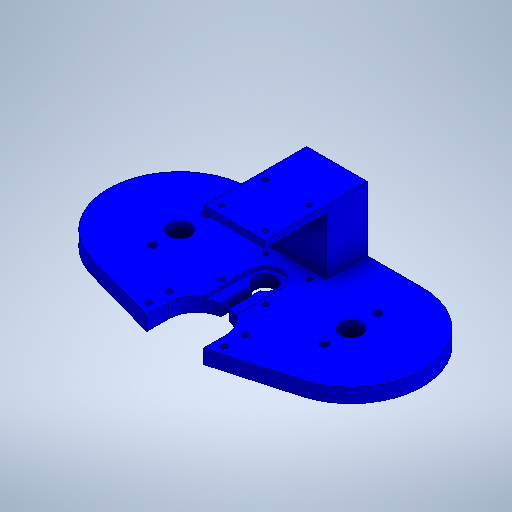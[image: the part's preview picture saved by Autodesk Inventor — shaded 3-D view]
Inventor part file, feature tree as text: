
AUTODESK INVENTOR PART (.ipt)
format: ipt  version: 2025.2 (Build 292293000, 293)  size: 375,808 bytes
history: native  units: mm
features: extrude x6, hole x4, sketch x3, other x1
ambient origin geometry x8: Origin, YZ Plane, XZ Plane, XY Plane, X Axis, Y Axis, Z Axis, Center Point
bodies: Body1 (feature_tree)
feature tree (14):
  sketch  "Sketch6"  dims[d37=120.0mm d38=60.0mm]
  extrude  "Extrusion8"  Depth=60.0mm
  hole  "Hole1"  [1 undecoded]
  hole  "Hole2"  [1 undecoded]
  extrude  "Extrusion10"  Depth=8.0mm
  extrude  "Extrusion11"  Depth=10.0mm TaperAngle=0.0deg
  extrude  "Extrusion12"  Depth=8.0mm
  extrude  "Extrusion13"  Depth=8.0mm
  other  "Work Axis1"
  hole  "Hole3"  [1 undecoded]
  extrude  "Extrusion14"  Depth=8.0mm
  hole  "Hole4"  [1 undecoded]
  sketch  "Sketch7"  dims[d39=100.0mm d40=100.0mm]
  sketch  "Sketch8"  dims[d41=15.0mm d42=15.0mm d43=15.0mm d44=10.0mm d45=0.0mm d46=37.3mm d47=37.3mm d48=30.759mm d49=30.759mm d50=30.759mm d51=3.5mm d52=6.0mm d53=4.0mm d54=2.0mm d55=90.0deg d56=8.0mm d57=20.594885mm d58=5.0mm d59=6.0mm d60=4.0mm d61=2.0mm d62=90.0deg d63=8.0mm d64=20.594885mm d65=42.3mm d66=43.0mm d67=50.0mm d70=6.0mm d71=200.0mm d72=15.0mm d73=0.0mm d74=45.0mm d75=0.0mm d76=22.5mm d77=200.0mm d78=2.0mm d79=0.0mm d80=5.0mm d81=43.0mm d82=0.0mm d83=30.759mm d84=30.759mm d85=3.5mm d86=6.0mm d87=4.0mm d88=2.0mm d89=90.0deg d90=8.0mm d91=20.594885mm d93=48.0mm d94=40.0mm d95=0.0mm d96=0.0mm d97=55.0mm d98=165.0deg d99=4.0mm d100=6.0mm d101=4.0mm d102=2.0mm d103=90.0deg d104=8.0mm d105=20.594885mm d5=0.5mm d6=0.872665mm d7=0.5mm d8=0.872665mm]
note: 4 required parameter values undecoded (feature->parameter linkage not recoverable at this tier; creation-order binding heuristic only, values carry confidence <= 0.55)
